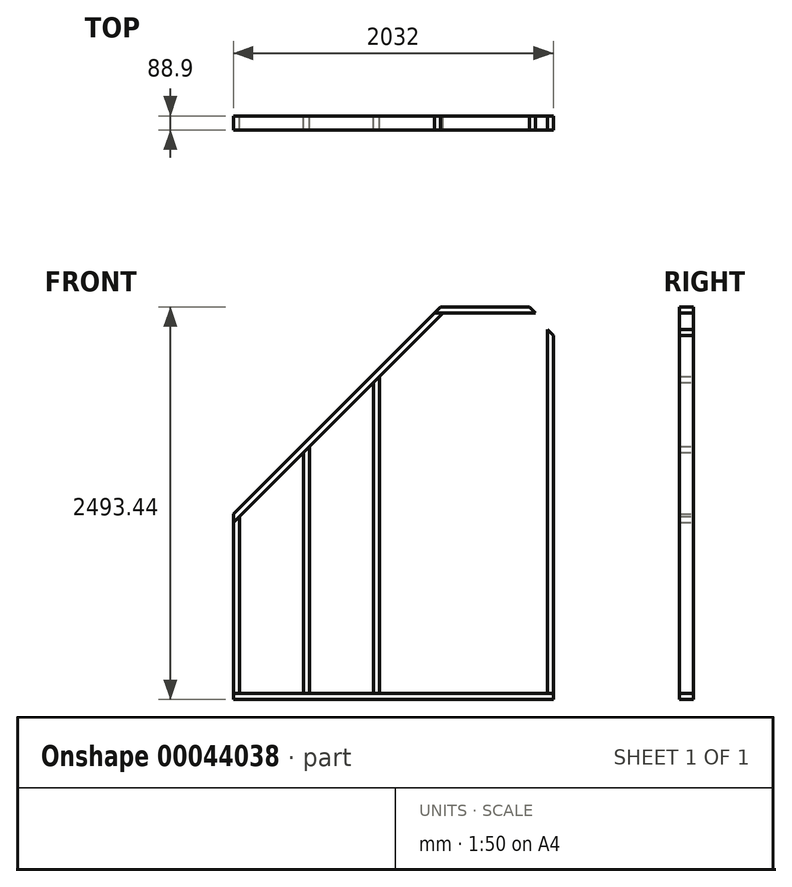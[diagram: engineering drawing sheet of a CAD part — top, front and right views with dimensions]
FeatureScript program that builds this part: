
annotation { "Feature Type Name" : "Feature", "Feature Type Description" : "" }
export const myFeature = defineFeature(function(context is Context, id is Id, definition is map)
    precondition{}
    {
        {
            var Q0;
            Q0=qCreatedBy(makeId("Front.planeOp"),FACE);
            var sketch = newSketch(context, id + "F0", { "sketchPlane" : qUnion([Q0])});
            skLineSegment(sketch, "E0", {"start": v(-320.68, 0) * mm, "end": v(320.68, 0) * mm});
            skLineSegment(sketch, "E1", {"start": v(320.68, 0) * mm, "end": v(282.57, 38.1) * mm});
            skLineSegment(sketch, "E2", {"start": v(282.57, 38.1) * mm, "end": v(-282.57, 38.1) * mm});
            skLineSegment(sketch, "E3", {"start": v(-282.57, 38.1) * mm, "end": v(-320.68, 0) * mm});
            skPoint(sketch, "E4", {"position": v(0, 38.1) * mm});
            skPoint(sketch, "E5", {"position": v(0, 0) * mm});
            skSolve(sketch);
        }
        {
            var Q0;
            Q0 = qSketchRegion(id + "F0", true);
            extrude(context, id + "F1", {"entities" : qUnion([Q0]), "depth" : 88.9 * mm, "symmetric" : true});
        }
        {
            var Q0;
            Q0=qCreatedBy(makeId("Front.planeOp"),FACE);
            var sketch = newSketch(context, id + "F2", { "sketchPlane" : qUnion([Q0])});
            skPoint(sketch, "E6.0", {"position": v(-282.57, 38.1) * mm});
            skPoint(sketch, "E7.0", {"position": v(-320.68, 0) * mm});
            skLineSegment(sketch, "E8.0", {"start": v(-320.68, 0) * mm, "end": v(320.68, 0) * mm});
            skLineSegment(sketch, "E9.0", {"start": v(-282.57, 38.1) * mm, "end": v(-320.68, 0) * mm});
            skLineSegment(sketch, "E10", {"start": v(-282.57, 38.1) * mm, "end": v(-1598.18, -1277.5) * mm});
            skLineSegment(sketch, "E11", {"start": v(-1598.18, -1277.5) * mm, "end": v(-1598.18, -1331.39) * mm});
            skLineSegment(sketch, "E12.0", {"start": v(282.57, 38.1) * mm, "end": v(-282.57, 38.1) * mm});
            skLineSegment(sketch, "E13", {"start": v(-1598.18, -1331.39) * mm, "end": v(-228.7, 38.1) * mm});
            skLineSegment(sketch, "E14", {"start": v(-228.7, 38.1) * mm, "end": v(-282.57, 38.1) * mm});
            skPoint(sketch, "E15", {"position": v(-266.8, 0) * mm});
            skSolve(sketch);
        }
        {
            var Q0;
            Q0 = qSketchRegion(id + "F2", true);
            extrude(context, id + "F3", {"entities" : qUnion([Q0]), "depth" : 88.9 * mm, "symmetric" : true});
        }
        {
            var Q0;
            Q0=qCreatedBy(makeId("Front.planeOp"),FACE);
            var sketch = newSketch(context, id + "F4", { "sketchPlane" : qUnion([Q0])});
            skLineSegment(sketch, "E16.0", {"start": v(-1598.18, -1277.5) * mm, "end": v(-1598.18, -1331.39) * mm});
            skLineSegment(sketch, "E17.0", {"start": v(-282.57, 38.1) * mm, "end": v(-1598.18, -1277.5) * mm});
            skLineSegment(sketch, "E18.0", {"start": v(-1598.18, -1331.39) * mm, "end": v(-228.7, 38.1) * mm});
            skLineSegment(sketch, "E19", {"start": v(-1598.18, -1277.5) * mm, "end": v(-1598.18, -2417.24) * mm});
            skLineSegment(sketch, "E20", {"start": v(-1598.18, -2417.24) * mm, "end": v(-1560.08, -2417.24) * mm});
            skLineSegment(sketch, "E21", {"start": v(-1560.08, -2417.24) * mm, "end": v(-1560.08, -1239.4) * mm});
            skLineSegment(sketch, "E22", {"start": v(-1560.08, -1239.4) * mm, "end": v(-1598.18, -1277.5) * mm});
            skPoint(sketch, "E23", {"position": v(-1560.08, -1293.29) * mm});
            skSolve(sketch);
        }
        {
            var Q0;
            Q0 = qSketchRegion(id + "F4", true);
            extrude(context, id + "F5", {"entities" : qUnion([Q0]), "depth" : 88.9 * mm, "symmetric" : true});
        }
        {
            var Q0;
            Q0=qCreatedBy(makeId("Front.planeOp"),FACE);
            var sketch = newSketch(context, id + "F6", { "sketchPlane" : qUnion([Q0])});
            skLineSegment(sketch, "E24.0", {"start": v(-1598.18, -2417.24) * mm, "end": v(-1560.08, -2417.24) * mm});
            skLineSegment(sketch, "E25.bottom", {"start": v(-1598.18, -2417.24) * mm, "end": v(433.82, -2417.24) * mm});
            skLineSegment(sketch, "E25.top", {"start": v(-1598.18, -2455.34) * mm, "end": v(433.82, -2455.34) * mm});
            skLineSegment(sketch, "E25.left", {"start": v(-1598.18, -2417.24) * mm, "end": v(-1598.18, -2455.34) * mm});
            skLineSegment(sketch, "E25.right", {"start": v(433.82, -2417.24) * mm, "end": v(433.82, -2455.34) * mm});
            skSolve(sketch);
        }
        {
            var Q0;
            Q0 = qSketchRegion(id + "F6", true);
            extrude(context, id + "F7", {"entities" : qUnion([Q0]), "depth" : 88.9 * mm, "symmetric" : true});
        }
        {
            var Q0;
            Q0=makeQuery(id+"F1.opExtrude","SWEPT_BODY",BODY,{"disambiguationData":[OSD([sQuery(id+"F0.wireOp",EDGE,"E0"),sQuery(id+"F0.wireOp",EDGE,"E1"),sQuery(id+"F0.wireOp",EDGE,"E2"),sQuery(id+"F0.wireOp",EDGE,"E3")])]});
            var Q1;
            Q1=makeQuery(id+"F3.opExtrude","SWEPT_BODY",BODY,{"disambiguationData":[OSD([sQuery(id+"F2.wireOp",EDGE,"E10"),sQuery(id+"F2.wireOp",EDGE,"E11"),sQuery(id+"F2.wireOp",EDGE,"E13"),sQuery(id+"F2.wireOp",EDGE,"E14")])]});
            booleanBodies(context, id + "F8", {"operationType" : BooleanOperationType.SUBTRACTION, "tools" : qUnion([Q0]), "targets" : qUnion([Q1]), "keepTools" : true});
        }
        {
            var Q0;
            Q0=makeQuery(id+"F3.opExtrude","SWEPT_BODY",BODY,{"disambiguationData":[OSD([sQuery(id+"F2.wireOp",EDGE,"E10"),sQuery(id+"F2.wireOp",EDGE,"E11"),sQuery(id+"F2.wireOp",EDGE,"E13"),sQuery(id+"F2.wireOp",EDGE,"E14")])]});
            var Q1;
            Q1=makeQuery(id+"F5.opExtrude","SWEPT_BODY",BODY,{"disambiguationData":[OSD([sQuery(id+"F4.wireOp",EDGE,"E19"),sQuery(id+"F4.wireOp",EDGE,"E20"),sQuery(id+"F4.wireOp",EDGE,"E21"),sQuery(id+"F4.wireOp",EDGE,"E22")])]});
            booleanBodies(context, id + "F9", {"operationType" : BooleanOperationType.SUBTRACTION, "tools" : qUnion([Q0]), "targets" : qUnion([Q1]), "keepTools" : true});
        }
        {
            var Q0;
            Q0=qCreatedBy(makeId("Front.planeOp"),FACE);
            var sketch = newSketch(context, id + "F10", { "sketchPlane" : qUnion([Q0])});
            skLineSegment(sketch, "E26.0", {"start": v(433.82, -2417.24) * mm, "end": v(433.82, -2455.34) * mm});
            skLineSegment(sketch, "E27.bottom", {"start": v(433.82, -2417.24) * mm, "end": v(395.72, -2417.24) * mm});
            skLineSegment(sketch, "E27.top", {"start": v(433.82, -143.94) * mm, "end": v(395.72, -143.94) * mm});
            skLineSegment(sketch, "E27.left", {"start": v(433.82, -2417.24) * mm, "end": v(433.82, -143.94) * mm});
            skLineSegment(sketch, "E27.right", {"start": v(395.72, -2417.24) * mm, "end": v(395.72, -143.94) * mm});
            skLineSegment(sketch, "E28", {"start": v(395.72, -143.94) * mm, "end": v(395.72, -105.84) * mm});
            skLineSegment(sketch, "E29", {"start": v(395.72, -105.84) * mm, "end": v(433.82, -143.94) * mm});
            skSolve(sketch);
        }
        {
            var Q0;
            Q0 = qSketchRegion(id + "F10", true);
            extrude(context, id + "F11", {"entities" : qUnion([Q0]), "depth" : 88.9 * mm, "symmetric" : true});
        }
        {
            var Q0;
            Q0=qCreatedBy(makeId("Front.planeOp"),FACE);
            var sketch = newSketch(context, id + "F18", { "sketchPlane" : qUnion([Q0])});
            skLineSegment(sketch, "E30.0.0", {"start": v(433.82, -2417.24) * mm, "end": v(-1598.18, -2417.24) * mm});
            skLineSegment(sketch, "E30.0.1", {"start": v(-1598.18, -2417.24) * mm, "end": v(-1598.18, -2455.34) * mm});
            skLineSegment(sketch, "E30.0.2", {"start": v(-1598.18, -2455.34) * mm, "end": v(433.82, -2455.34) * mm});
            skLineSegment(sketch, "E30.0.3", {"start": v(433.82, -2455.34) * mm, "end": v(433.82, -2417.24) * mm});
            skLineSegment(sketch, "E30.0.4", {"start": v(433.82, -143.94) * mm, "end": v(395.72, -105.84) * mm});
            skLineSegment(sketch, "E30.0.5", {"start": v(395.72, -105.84) * mm, "end": v(395.72, -2417.24) * mm});
            skLineSegment(sketch, "E31.bottom", {"start": v(-643.26, -2417.24) * mm, "end": v(95.67, -2417.24) * mm});
            skLineSegment(sketch, "E31.top", {"start": v(-643.26, -1677.64) * mm, "end": v(95.67, -1677.64) * mm});
            skLineSegment(sketch, "E31.left", {"start": v(-643.26, -2417.24) * mm, "end": v(-643.26, -1677.64) * mm});
            skLineSegment(sketch, "E31.right", {"start": v(95.67, -2417.24) * mm, "end": v(95.67, -1677.64) * mm});
            skSolve(sketch);
        }
        {
            var Q0;
            Q0=qCreatedBy(makeId("Front.planeOp"),FACE);
            var sketch = newSketch(context, id + "F12", { "sketchPlane" : qUnion([Q0])});
            skLineSegment(sketch, "E32.0", {"start": v(433.82, -2417.24) * mm, "end": v(-1598.18, -2417.24) * mm});
            skLineSegment(sketch, "E33.0", {"start": v(-1560.08, -2417.24) * mm, "end": v(-1560.08, -1293.29) * mm});
            skLineSegment(sketch, "E34", {"start": v(-1153.68, -2417.24) * mm, "end": v(-1153.68, -886.89) * mm});
            skLineSegment(sketch, "E35", {"start": v(-1115.58, -2417.24) * mm, "end": v(-1115.58, -848.79) * mm});
            skLineSegment(sketch, "E36", {"start": v(-1115.58, -848.79) * mm, "end": v(-1153.68, -886.89) * mm});
            skSolve(sketch);
        }
        {
            var Q0;
            Q0 = qSketchRegion(id + "F12", true);
            extrude(context, id + "F13", {"entities" : qUnion([Q0]), "depth" : 88.9 * mm, "symmetric" : true});
        }
        {
            var Q0;
            Q0=qCreatedBy(makeId("Front.planeOp"),FACE);
            var sketch = newSketch(context, id + "F14", { "sketchPlane" : qUnion([Q0])});
            skLineSegment(sketch, "E37.0", {"start": v(433.82, -2417.24) * mm, "end": v(-1598.18, -2417.24) * mm});
            skLineSegment(sketch, "E38.0", {"start": v(-1115.58, -2417.24) * mm, "end": v(-1115.58, -848.79) * mm});
            skLineSegment(sketch, "E39", {"start": v(-709.18, -2417.24) * mm, "end": v(-709.18, -442.39) * mm});
            skLineSegment(sketch, "E40", {"start": v(-671.08, -2417.24) * mm, "end": v(-671.08, -404.29) * mm});
            skLineSegment(sketch, "E41", {"start": v(-709.18, -442.39) * mm, "end": v(-671.08, -404.29) * mm});
            skSolve(sketch);
        }
        {
            var Q0;
            Q0 = qSketchRegion(id + "F14", true);
            extrude(context, id + "F15", {"entities" : qUnion([Q0]), "depth" : 88.9 * mm, "symmetric" : true});
        }
    });
